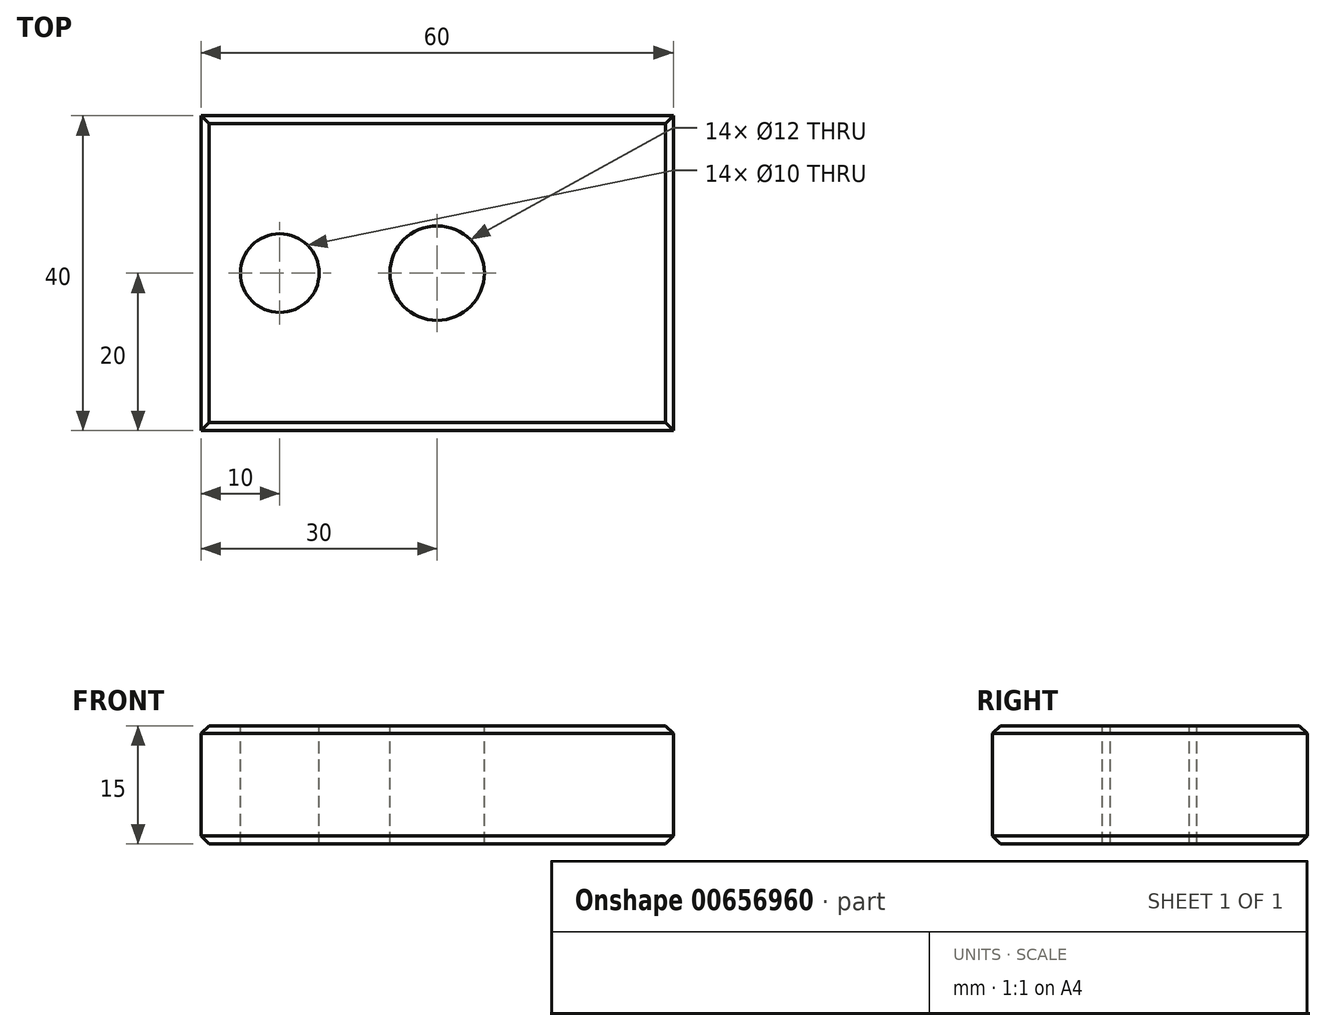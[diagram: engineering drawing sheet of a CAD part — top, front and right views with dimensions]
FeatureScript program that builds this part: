
annotation { "Feature Type Name" : "Feature", "Feature Type Description" : "" }
export const myFeature = defineFeature(function(context is Context, id is Id, definition is map)
    precondition{}
    {
        {
            var Q0;
            Q0=qCreatedBy(makeId("Top.planeOp"),FACE);
            var sketch = newSketch(context, id + "F0", { "sketchPlane" : qUnion([Q0])});
            skLineSegment(sketch, "E0.bottom", {"start": v(30, 20) * mm, "end": v(-30, 20) * mm});
            skLineSegment(sketch, "E0.top", {"start": v(30, -20) * mm, "end": v(-30, -20) * mm});
            skLineSegment(sketch, "E0.left", {"start": v(30, 20) * mm, "end": v(30, -20) * mm});
            skLineSegment(sketch, "E0.right", {"start": v(-30, 20) * mm, "end": v(-30, -20) * mm});
            skPoint(sketch, "E0.middle", {"position": v(0, 0) * mm});
            skSolve(sketch);
        }
        {
            var Q0;
            Q0=makeQuery(id+"F0.imprint","IMPRINT",FACE,{"disambiguationData":[TD([[makeQuery(id+"F0.imprint","IMPRINT",EDGE,{"derivedFrom":sQuery(id+"F0.wireOp",EDGE,"E0.bottom")}),1.0]])]});
            extrude(context, id + "F1", {"entities" : qUnion([Q0]), "oppositeDirection" : true, "depth" : 15 * mm, "offsetDistance" : 25 * mm});
        }
        {
            var Q0;
            Q0=makeQuery(id+"F1.opExtrude","CAP_FACE",FACE,{"disambiguationData":[OSD([sQuery(id+"F0.wireOp",EDGE,"E0.bottom"),sQuery(id+"F0.wireOp",EDGE,"E0.top"),sQuery(id+"F0.wireOp",EDGE,"E0.left"),sQuery(id+"F0.wireOp",EDGE,"E0.right")])],"isStart":true});
            var Q1;
            Q1=makeQuery(id+"F1.opExtrude","CAP_FACE",FACE,{"disambiguationData":[OSD([sQuery(id+"F0.wireOp",EDGE,"E0.bottom"),sQuery(id+"F0.wireOp",EDGE,"E0.top"),sQuery(id+"F0.wireOp",EDGE,"E0.left"),sQuery(id+"F0.wireOp",EDGE,"E0.right")])],"isStart":false});
            chamfer(context, id + "F2", {"entities" : qUnion([Q0, Q1]), "width" : 1 * mm, "tangentPropagation" : true});
        }
        {
            var Q0;
            Q0=makeQuery(id+"F1.opExtrude","CAP_FACE",FACE,{"disambiguationData":[OSD([sQuery(id+"F0.wireOp",EDGE,"E0.bottom"),sQuery(id+"F0.wireOp",EDGE,"E0.top"),sQuery(id+"F0.wireOp",EDGE,"E0.left"),sQuery(id+"F0.wireOp",EDGE,"E0.right")])],"isStart":true});
            var sketch = newSketch(context, id + "F3", { "sketchPlane" : qUnion([Q0])});
            skCircle(sketch, "E1", {"center": v(-20, 0) * mm, "radius": 5 * mm});
            skCircle(sketch, "E2", {"center": v(0, 0) * mm, "radius": 6 * mm});
            skSolve(sketch);
        }
        {
            var Q0;
            Q0=makeQuery(id+"F3.imprint","IMPRINT",FACE,{"disambiguationData":[TD([[makeQuery(id+"F3.imprint","IMPRINT",EDGE,{"derivedFrom":sQuery(id+"F3.wireOp",EDGE,"E1")}),1.0]])]});
            var Q1;
            Q1=makeQuery(id+"F3.imprint","IMPRINT",FACE,{"disambiguationData":[TD([[makeQuery(id+"F3.imprint","IMPRINT",EDGE,{"derivedFrom":sQuery(id+"F3.wireOp",EDGE,"E2")}),1.0]])]});
            extrude(context, id + "F4", {"entities" : qUnion([Q0, Q1]), "operationType" : NewBodyOperationType.REMOVE, "endBound" : BoundingType.THROUGH_ALL, "oppositeDirection" : true, "depth" : 25 * mm, "offsetDistance" : 25 * mm});
        }
    });
